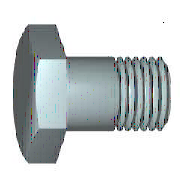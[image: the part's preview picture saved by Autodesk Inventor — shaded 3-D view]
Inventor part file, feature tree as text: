
AUTODESK INVENTOR PART (.ipt)
format: ipt  version: 2021 (Build 250183000, 183)  size: 189,440 bytes
history: native  units: mm (DEFAULTED — no unit token found)
features: sketch x3, extrude x1, chamfer x1, plane x1
ambient origin geometry x7: Origin, YZ Plane, XZ Plane, X Axis, Y Axis, Z Axis, Center Point
bodies: Solid1 (feature_tree), Body (feature_tree)
feature tree (6):
  extrude  "Head"  Depth=18.0mm
  chamfer  "Chamfer1"  Distance=3.5mm
  plane  "Work Plane1"
  sketch  "Sketch1"  dims[d0=60.0mm d1=18.0mm]
  sketch  "Sketch2"  dims[d2=6.0mm]
  sketch  "Sketch4"  dims[d12=90.0deg d3=3.5mm d4=0.0mm d5=30.0deg d21=90.0deg d6=0.61345mm d7=0.61355mm d8=0.0mm d9=0.5001mm d10=8.88mm d11=10.0mm d13=0.61355mm d14=6.0mm d15=18.0mm d16=0.0mm d19=10.0mm d55=45.0deg d57=0.0mm d58=0.0mm]
